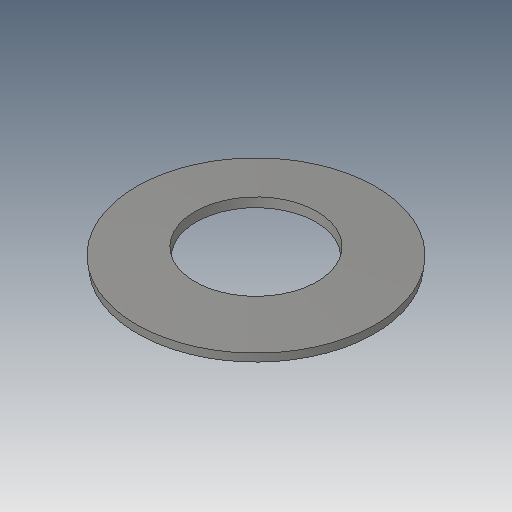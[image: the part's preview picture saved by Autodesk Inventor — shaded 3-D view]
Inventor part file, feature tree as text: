
AUTODESK INVENTOR PART (.ipt)
format: ipt  version: 2019 (Build 230136000, 136)  size: 94,720 bytes
history: native  units: in
note: dims shown in document units (in); Inventor stores cm internally (conversion verified against a paired STEP export)
features: revolve x1
ambient origin geometry x8: Origin, YZ Plane, XZ Plane, XY Plane, X Axis, Y Axis, Z Axis, Center Point
bodies: Solid1 (feature_tree)
feature tree (1):
  revolve  "Revolve1"  [1 undecoded]
note: 1 required parameter value undecoded (feature->parameter linkage not recoverable at this tier; creation-order binding heuristic only, values carry confidence <= 0.55)
